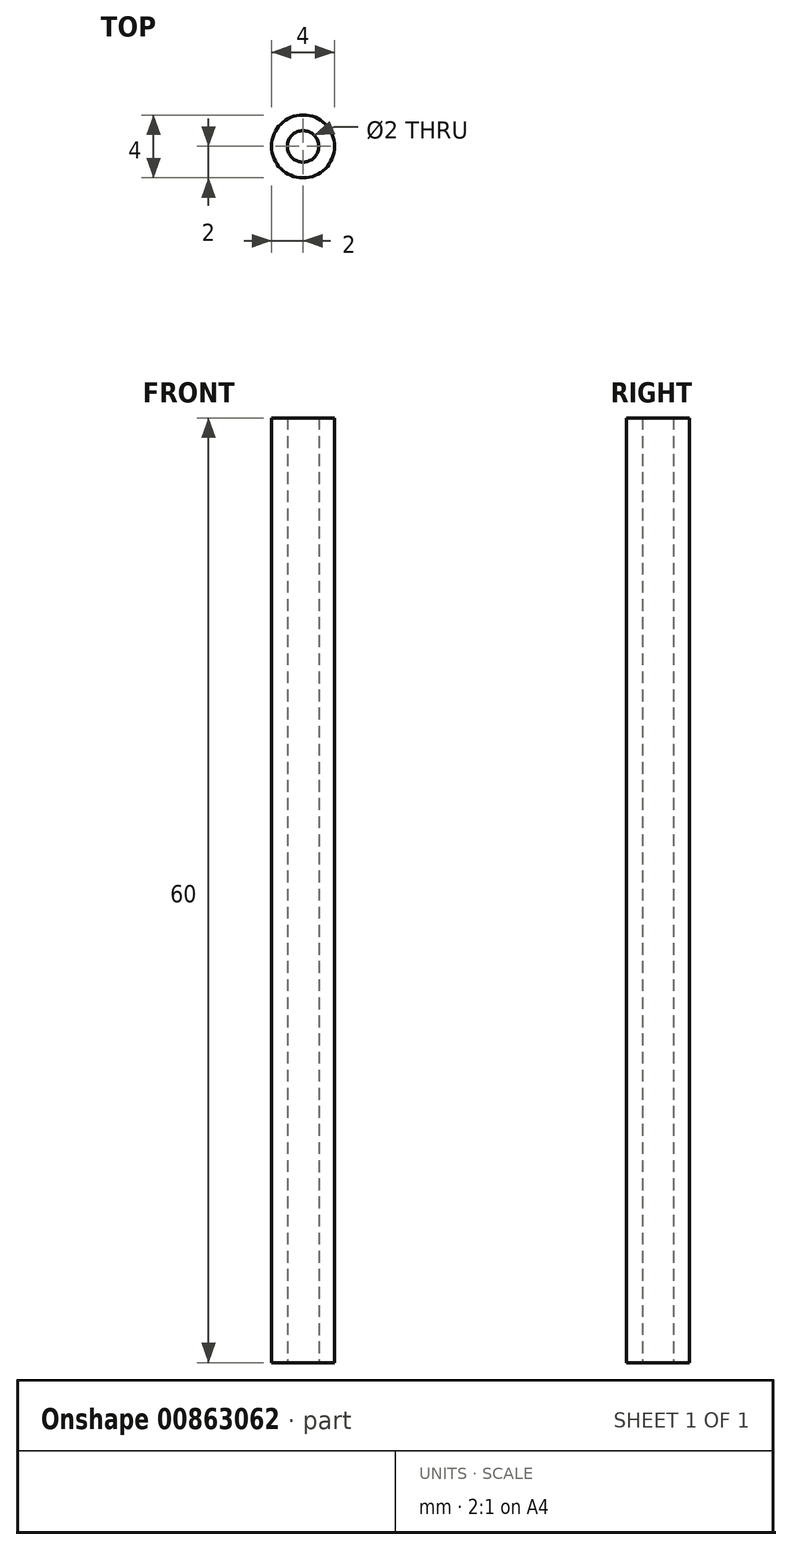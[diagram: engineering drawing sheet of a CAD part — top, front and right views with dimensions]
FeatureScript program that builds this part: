
annotation { "Feature Type Name" : "Feature", "Feature Type Description" : "" }
export const myFeature = defineFeature(function(context is Context, id is Id, definition is map)
    precondition{}
    {
        {
            var Q0;
            Q0=qCreatedBy(makeId("Top.planeOp"),FACE);
            var sketch = newSketch(context, id + "F0", { "sketchPlane" : qUnion([Q0])});
            skCircle(sketch, "E0", {"center": v(0, 0) * mm, "radius": 1 * mm});
            skCircle(sketch, "E1", {"center": v(0, 0) * mm, "radius": 2 * mm});
            skSolve(sketch);
        }
        {
            var Q0;
            Q0=makeQuery(id+"F0.imprint","IMPRINT",FACE,{"disambiguationData":[TD([[makeQuery(id+"F0.imprint","IMPRINT",EDGE,{"derivedFrom":sQuery(id+"F0.wireOp",EDGE,"E0")}),-1.0]])]});
            extrude(context, id + "F1", {"entities" : qUnion([Q0]), "depth" : 60 * mm, "offsetDistance" : 25 * mm});
        }
    });
